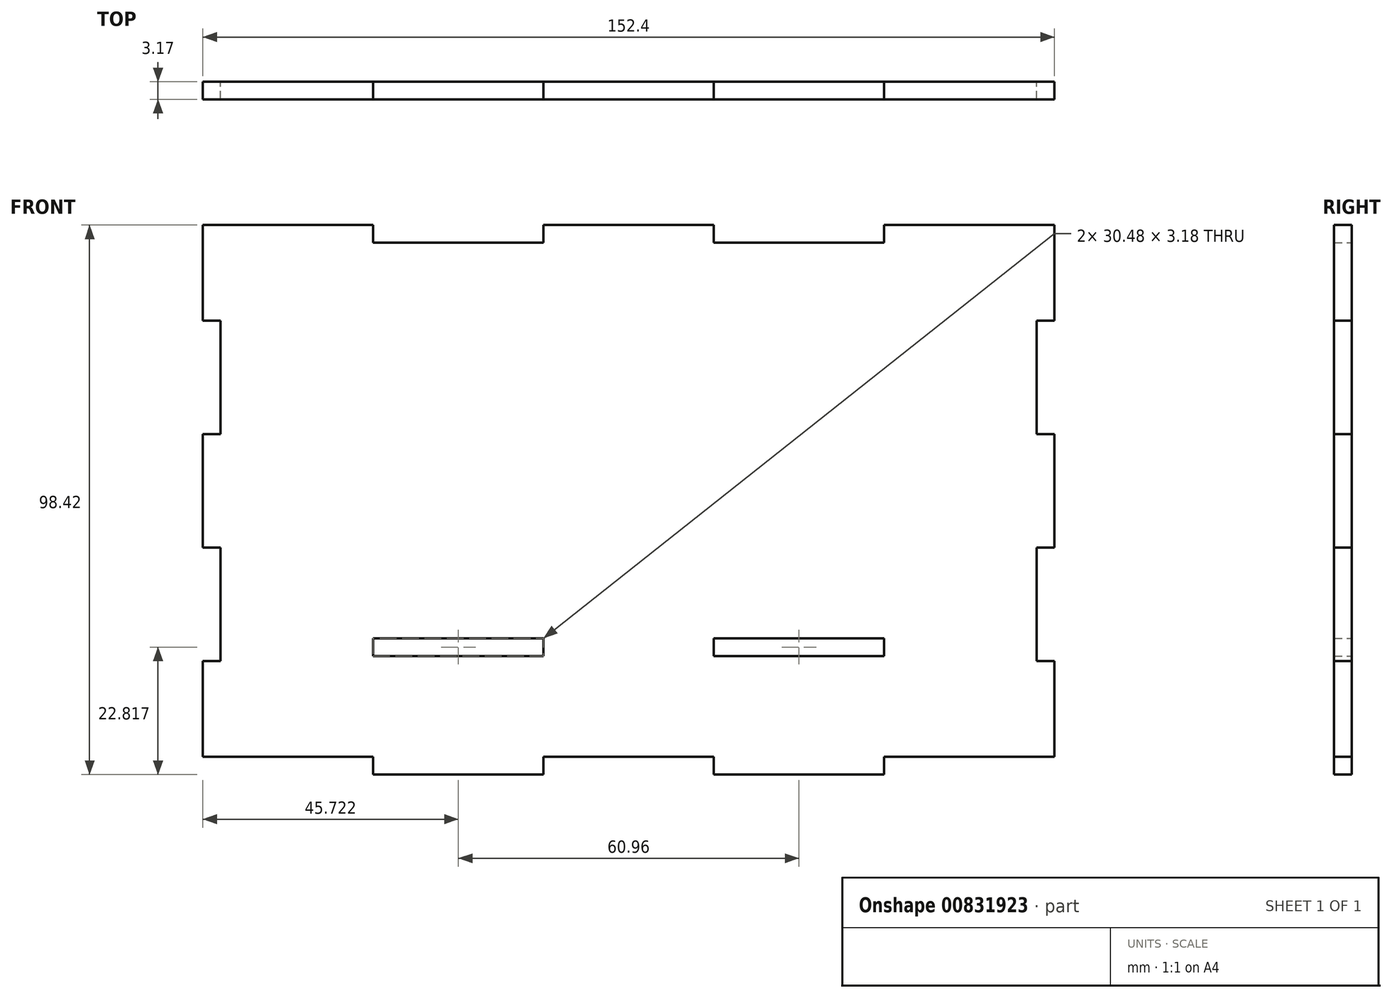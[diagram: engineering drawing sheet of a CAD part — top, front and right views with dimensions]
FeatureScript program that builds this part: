
annotation { "Feature Type Name" : "Feature", "Feature Type Description" : "" }
export const myFeature = defineFeature(function(context is Context, id is Id, definition is map)
    precondition{}
    {
        {
            var Q0;
            Q0=qCreatedBy(makeId("Front.planeOp"),FACE);
            var sketch = newSketch(context, id + "F0", { "sketchPlane" : qUnion([Q0])});
            skLineSegment(sketch, "E0", {"start": v(-308.78, 0) * mm, "end": v(-278.3, 0) * mm});
            skLineSegment(sketch, "E1", {"start": v(-278.3, 0) * mm, "end": v(-278.3, -3.17) * mm});
            skLineSegment(sketch, "E2", {"start": v(-278.3, -3.18) * mm, "end": v(-247.82, -3.18) * mm});
            skLineSegment(sketch, "E3", {"start": v(-247.82, -3.17) * mm, "end": v(-247.82, 0) * mm});
            skLineSegment(sketch, "E4", {"start": v(-247.82, 0) * mm, "end": v(-217.34, 0) * mm});
            skLineSegment(sketch, "E5", {"start": v(-217.34, 0) * mm, "end": v(-217.34, -3.17) * mm});
            skLineSegment(sketch, "E6", {"start": v(-217.34, -3.17) * mm, "end": v(-186.86, -3.17) * mm});
            skLineSegment(sketch, "E7", {"start": v(-186.86, -3.17) * mm, "end": v(-186.86, 0) * mm});
            skLineSegment(sketch, "E8", {"start": v(-186.86, 0) * mm, "end": v(-156.38, 0) * mm});
            skLineSegment(sketch, "E9", {"start": v(-156.38, 0) * mm, "end": v(-156.38, 17.15) * mm});
            skLineSegment(sketch, "E10", {"start": v(-156.38, 17.15) * mm, "end": v(-159.55, 17.15) * mm});
            skLineSegment(sketch, "E11", {"start": v(-159.55, 17.15) * mm, "end": v(-159.55, 37.47) * mm});
            skLineSegment(sketch, "E12", {"start": v(-159.55, 37.47) * mm, "end": v(-156.38, 37.47) * mm});
            skLineSegment(sketch, "E13", {"start": v(-156.38, 37.47) * mm, "end": v(-156.38, 57.79) * mm});
            skLineSegment(sketch, "E14", {"start": v(-156.38, 57.79) * mm, "end": v(-159.55, 57.79) * mm});
            skLineSegment(sketch, "E15", {"start": v(-159.55, 57.79) * mm, "end": v(-159.55, 78.1) * mm});
            skLineSegment(sketch, "E16", {"start": v(-159.55, 78.1) * mm, "end": v(-156.38, 78.1) * mm});
            skLineSegment(sketch, "E17", {"start": v(-156.38, 78.1) * mm, "end": v(-156.38, 95.25) * mm});
            skLineSegment(sketch, "E18", {"start": v(-156.38, 95.25) * mm, "end": v(-186.86, 95.25) * mm});
            skLineSegment(sketch, "E19", {"start": v(-186.86, 95.25) * mm, "end": v(-186.86, 92.08) * mm});
            skLineSegment(sketch, "E20", {"start": v(-186.86, 92.08) * mm, "end": v(-217.34, 92.08) * mm});
            skLineSegment(sketch, "E21", {"start": v(-217.34, 92.08) * mm, "end": v(-217.34, 95.25) * mm});
            skLineSegment(sketch, "E22", {"start": v(-217.34, 95.25) * mm, "end": v(-247.82, 95.25) * mm});
            skLineSegment(sketch, "E23", {"start": v(-247.82, 95.25) * mm, "end": v(-247.82, 92.08) * mm});
            skLineSegment(sketch, "E24", {"start": v(-247.82, 92.08) * mm, "end": v(-278.3, 92.08) * mm});
            skLineSegment(sketch, "E25", {"start": v(-278.3, 92.08) * mm, "end": v(-278.3, 95.25) * mm});
            skLineSegment(sketch, "E26", {"start": v(-278.3, 95.25) * mm, "end": v(-308.78, 95.25) * mm});
            skLineSegment(sketch, "E27", {"start": v(-308.78, 95.25) * mm, "end": v(-308.78, 78.1) * mm});
            skLineSegment(sketch, "E28", {"start": v(-308.78, 78.1) * mm, "end": v(-305.6, 78.1) * mm});
            skLineSegment(sketch, "E29", {"start": v(-305.6, 78.1) * mm, "end": v(-305.6, 57.79) * mm});
            skLineSegment(sketch, "E30", {"start": v(-305.6, 57.79) * mm, "end": v(-308.78, 57.79) * mm});
            skLineSegment(sketch, "E31", {"start": v(-308.78, 57.79) * mm, "end": v(-308.78, 37.47) * mm});
            skLineSegment(sketch, "E32", {"start": v(-308.78, 37.47) * mm, "end": v(-305.6, 37.47) * mm});
            skLineSegment(sketch, "E33", {"start": v(-305.6, 37.47) * mm, "end": v(-305.6, 17.15) * mm});
            skLineSegment(sketch, "E34", {"start": v(-305.6, 17.15) * mm, "end": v(-308.78, 17.15) * mm});
            skLineSegment(sketch, "E35", {"start": v(-308.78, 17.15) * mm, "end": v(-308.78, 0) * mm});
            skLineSegment(sketch, "E36.bottom", {"start": v(-278.3, 21.23) * mm, "end": v(-247.82, 21.23) * mm});
            skLineSegment(sketch, "E36.top", {"start": v(-278.3, 18.06) * mm, "end": v(-247.82, 18.06) * mm});
            skLineSegment(sketch, "E36.left", {"start": v(-278.3, 21.23) * mm, "end": v(-278.3, 18.06) * mm});
            skLineSegment(sketch, "E36.right", {"start": v(-247.82, 21.23) * mm, "end": v(-247.82, 18.06) * mm});
            skLineSegment(sketch, "E37.bottom", {"start": v(-217.34, 21.23) * mm, "end": v(-186.86, 21.23) * mm});
            skLineSegment(sketch, "E37.top", {"start": v(-217.34, 18.06) * mm, "end": v(-186.86, 18.06) * mm});
            skLineSegment(sketch, "E37.left", {"start": v(-217.34, 21.23) * mm, "end": v(-217.34, 18.06) * mm});
            skLineSegment(sketch, "E37.right", {"start": v(-186.86, 21.23) * mm, "end": v(-186.86, 18.06) * mm});
            skSolve(sketch);
        }
        {
            var Q0;
            Q0=makeQuery(id+"F0.imprint","IMPRINT",FACE,{"disambiguationData":[TD([[makeQuery(id+"F0.imprint","IMPRINT",EDGE,{"derivedFrom":sQuery(id+"F0.wireOp",EDGE,"E0")}),1.0]])]});
            extrude(context, id + "F1", {"entities" : qUnion([Q0]), "depth" : 3.17 * mm, "offsetDistance" : 25.4 * mm});
        }
    });
